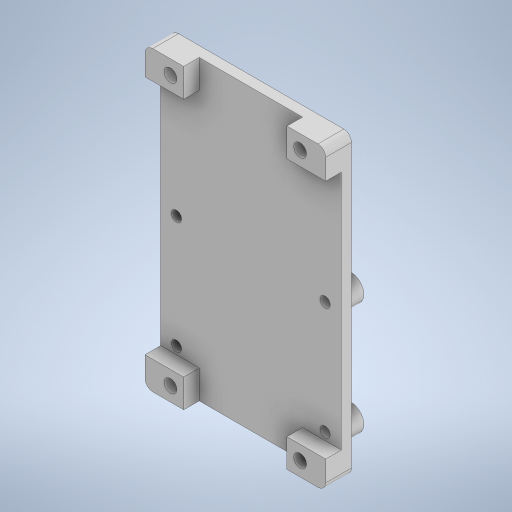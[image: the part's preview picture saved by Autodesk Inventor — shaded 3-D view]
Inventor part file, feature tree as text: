
AUTODESK INVENTOR PART (.ipt)
format: ipt  version: 2023 (Build 270158000, 158)  size: 338,432 bytes
history: native  units: mm
features: sketch x5, extrude x5, projected_geometry x3, other x1, hole x1
ambient origin geometry x8: Origin, YZ Plane, XZ Plane, XY Plane, X Axis, Y Axis, Z Axis, Center Point
bodies: Body1 (feature_tree)
feature tree (15):
  other  "솔리드1"
  sketch  "스케치1"
  extrude  "돌출1"  Depth=35.0mm
  extrude  "돌출2"  Depth=57.6mm
  sketch  "스케치3"
  extrude  "돌출3"  Depth=25.1mm
  extrude  "돌출4"  Depth=52.1mm
  extrude  "돌출5"  Depth=2.5mm
  hole  "구멍2"  [1 undecoded]
  sketch  "스케치4"
  sketch  "스케치5"
  sketch  "스케치6"
  projected_geometry  "투영된 루프1"
  projected_geometry  "투영된 루프2"
  projected_geometry  "투영된 루프3"
note: 1 required parameter value undecoded (feature->parameter linkage not recoverable at this tier; creation-order binding heuristic only, values carry confidence <= 0.55)
